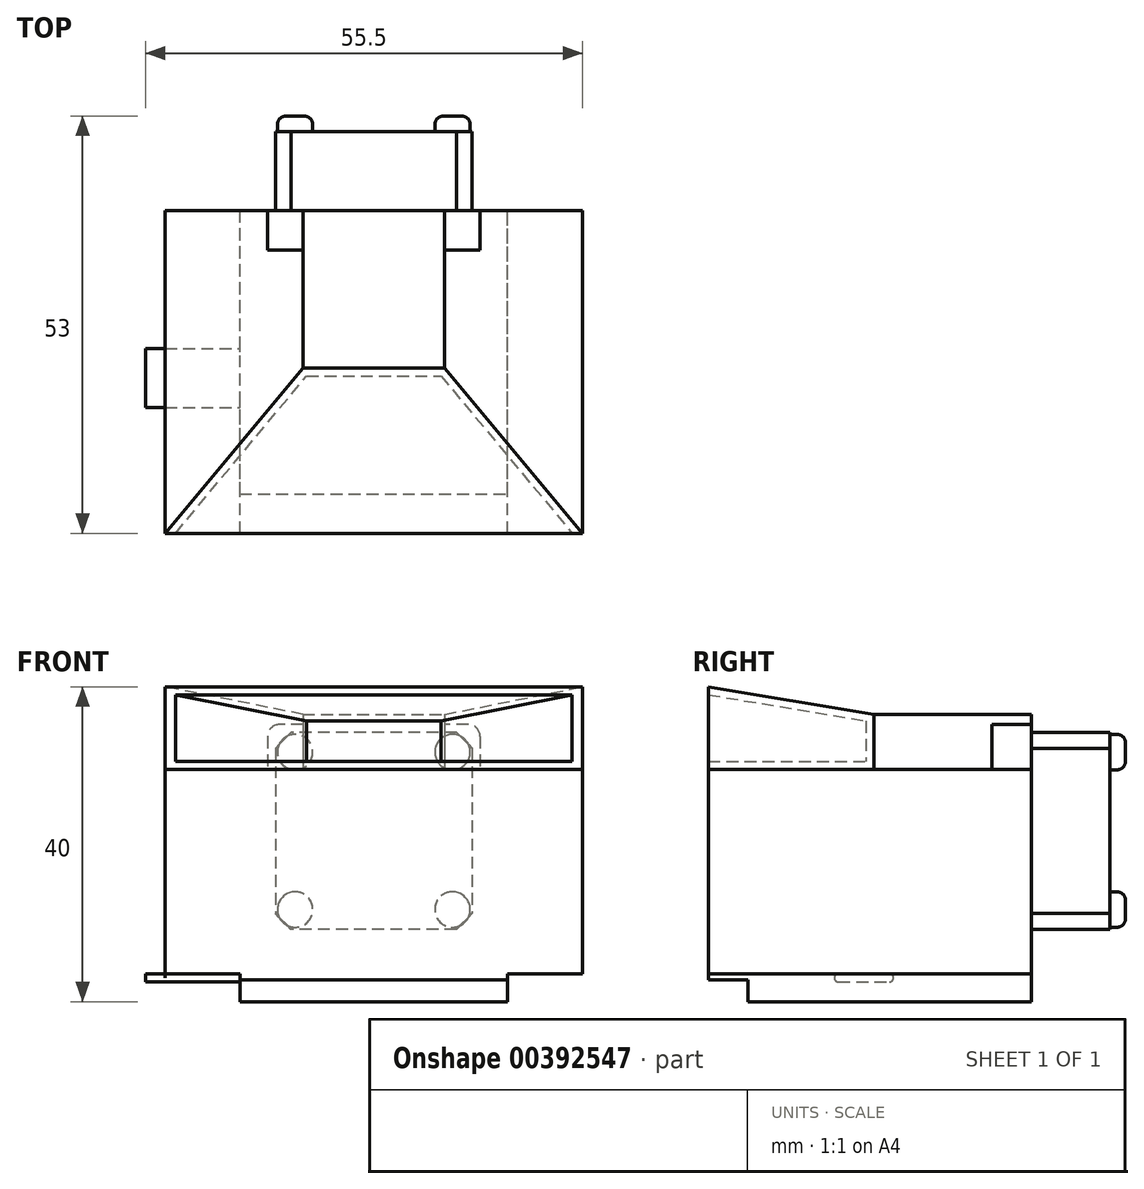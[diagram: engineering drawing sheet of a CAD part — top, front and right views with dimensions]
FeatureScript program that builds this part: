
annotation { "Feature Type Name" : "Feature", "Feature Type Description" : "" }
export const myFeature = defineFeature(function(context is Context, id is Id, definition is map)
    precondition{}
    {
        {
            var Q0;
            Q0=qCreatedBy(makeId("Front.planeOp"),FACE);
            var sketch = newSketch(context, id + "F0", { "sketchPlane" : qUnion([Q0])});
            skLineSegment(sketch, "E0.bottom", {"start": v(-26.5, -13) * mm, "end": v(26.5, -13) * mm});
            skLineSegment(sketch, "E0.top", {"start": v(-26.5, 13) * mm, "end": v(26.5, 13) * mm});
            skLineSegment(sketch, "E0.left", {"start": v(-26.5, -13) * mm, "end": v(-26.5, 13) * mm});
            skLineSegment(sketch, "E0.right", {"start": v(26.5, -13) * mm, "end": v(26.5, 13) * mm});
            skPoint(sketch, "E1", {"position": v(-26.5, 0) * mm});
            skPoint(sketch, "E2", {"position": v(0, -13) * mm});
            skSolve(sketch);
        }
        {
            var Q0;
            {var subQ0=sQuery(id+"F0.wireOp",EDGE,"lT0iIPiZ-68E4-k4fb-Xnzf-Mz2QpFusgy4Y.top");Q0=makeQuery(id+"F0.imprint","IMPRINT",FACE,{"disambiguationData":[TD([[makeQuery(id+"F0.imprint","IMPRINT",EDGE,{"derivedFrom":subQ0}),1.0]])]});}
            var Q1;
            Q1=makeQuery(id+"F0.imprint","IMPRINT",FACE,{"disambiguationData":[TD([[makeQuery(id+"F0.imprint","IMPRINT",EDGE,{"derivedFrom":sQuery(id+"F0.wireOp",EDGE,"E0.bottom")}),1.0]])]});
            extrude(context, id + "F1", {"entities" : qUnion([Q0, Q1]), "oppositeDirection" : true, "depth" : 41 * mm});
        }
        {
            var Q0;
            Q0=makeQuery(id+"F1.opExtrude","SWEPT_FACE",FACE,{"disambiguationData":[OSD([sQuery(id+"F0.wireOp",EDGE,"E0.top")])]});
            var sketch = newSketch(context, id + "F2", { "sketchPlane" : qUnion([Q0])});
            skLineSegment(sketch, "E3.bottom", {"start": v(-9, 41) * mm, "end": v(9, 41) * mm});
            skLineSegment(sketch, "E3.top", {"start": v(-9, 21) * mm, "end": v(9, 21) * mm});
            skLineSegment(sketch, "E3.left", {"start": v(-9, 41) * mm, "end": v(-9, 21) * mm});
            skLineSegment(sketch, "E3.right", {"start": v(9, 41) * mm, "end": v(9, 21) * mm});
            skPoint(sketch, "E4", {"position": v(0, 41) * mm});
            skSolve(sketch);
        }
        {
            var Q0;
            Q0=makeQuery(id+"F2.imprint","IMPRINT",FACE,{"disambiguationData":[TD([[makeQuery(id+"F2.imprint","IMPRINT",EDGE,{"derivedFrom":sQuery(id+"F2.wireOp",EDGE,"E3.bottom")}),-1.0]])]});
            extrude(context, id + "F3", {"entities" : qUnion([Q0]), "operationType" : NewBodyOperationType.ADD, "depth" : 7 * mm});
        }
        {
            var Q0;
            Q0=makeQuery(id+"F0.imprint","IMPRINT",FACE,{"disambiguationData":[TD([[makeQuery(id+"F0.imprint","IMPRINT",EDGE,{"derivedFrom":sQuery(id+"F0.wireOp",EDGE,"E0.bottom")}),1.0]])]});
            var sketch = newSketch(context, id + "F4", { "sketchPlane" : qUnion([Q0])});
            skLineSegment(sketch, "E5.bottom", {"start": v(-26.5, 13) * mm, "end": v(26.5, 13) * mm});
            skLineSegment(sketch, "E5.top", {"start": v(-26.5, 23.5) * mm, "end": v(26.5, 23.5) * mm});
            skLineSegment(sketch, "E5.left", {"start": v(-26.5, 13) * mm, "end": v(-26.5, 23.5) * mm});
            skLineSegment(sketch, "E5.right", {"start": v(26.5, 13) * mm, "end": v(26.5, 23.5) * mm});
            skSolve(sketch);
        }
        {
            var Q1;
            Q1=makeQuery(id+"F3.opExtrude","SWEPT_FACE",FACE,{"disambiguationData":[OSD([sQuery(id+"F2.wireOp",EDGE,"E3.top")])]});
            var Q2;
            Q2=makeQuery(id+"F4.imprint","IMPRINT",FACE,{"disambiguationData":[TD([[makeQuery(id+"F4.imprint","IMPRINT",EDGE,{"derivedFrom":sQuery(id+"F4.wireOp",EDGE,"E5.bottom")}),1.0]])]});
            loft(context, id + "F5", {"sheetProfilesArray" : [{ "sheetProfileEntities" : qUnion([Q1]) }, { "sheetProfileEntities" : qUnion([Q2]) }]});
        }
        {
            var Q0;
            Q0=makeQuery(id+"F5.opLoft","CAP_FACE",FACE,{"disambiguationData":[OSD([makeQuery(id+"F4.imprint","IMPRINT",FACE,{"disambiguationData":[TD([[makeQuery(id+"F4.imprint","IMPRINT",EDGE,{"derivedFrom":sQuery(id+"F4.wireOp",EDGE,"E5.bottom")}),1.0]])]})])],"isStart":true});
            shell(context, id + "F6", {"entities" : qUnion([Q0]), "thickness" : 1 * mm});
        }
        {
            var Q0;
            Q0=makeQuery(id+"F1.opExtrude","SWEPT_FACE",FACE,{"disambiguationData":[OSD([sQuery(id+"F0.wireOp",EDGE,"E0.bottom")])]});
            var sketch = newSketch(context, id + "F7", { "sketchPlane" : qUnion([Q0])});
            skLineSegment(sketch, "E6.bottom", {"start": v(-17, 0) * mm, "end": v(17, 0) * mm});
            skLineSegment(sketch, "E6.top", {"start": v(-17, -5) * mm, "end": v(17, -5) * mm});
            skLineSegment(sketch, "E6.left", {"start": v(-17, 0) * mm, "end": v(-17, -5) * mm});
            skLineSegment(sketch, "E6.right", {"start": v(17, 0) * mm, "end": v(17, -5) * mm});
            skLineSegment(sketch, "E7.top", {"start": v(-17, -41) * mm, "end": v(17, -41) * mm});
            skLineSegment(sketch, "E7.left", {"start": v(-17, -5) * mm, "end": v(-17, -41) * mm});
            skLineSegment(sketch, "E7.right", {"start": v(17, -5) * mm, "end": v(17, -41) * mm});
            skPoint(sketch, "E8", {"position": v(0, 0) * mm});
            skSolve(sketch);
        }
        {
            var Q0;
            Q0=makeQuery(id+"F7.imprint","IMPRINT",FACE,{"disambiguationData":[TD([[makeQuery(id+"F7.imprint","IMPRINT",EDGE,{"derivedFrom":sQuery(id+"F7.wireOp",EDGE,"E6.bottom")}),-1.0]])]});
            extrude(context, id + "F8", {"entities" : qUnion([Q0]), "operationType" : NewBodyOperationType.ADD, "depth" : 0.7 * mm});
        }
        {
            var Q0;
            Q0=makeQuery(id+"F7.imprint","IMPRINT",FACE,{"disambiguationData":[TD([[makeQuery(id+"F7.imprint","IMPRINT",EDGE,{"derivedFrom":sQuery(id+"F7.wireOp",EDGE,"E6.top")}),-1.0]])]});
            extrude(context, id + "F9", {"entities" : qUnion([Q0]), "operationType" : NewBodyOperationType.ADD, "depth" : 3.5 * mm});
        }
        {
            var Q0;
            Q0=makeQuery(id+"F9.boolean.opBoolean","MERGE",FACE,{"derivedFrom":[makeQuery(id+"F3.boolean.opBoolean","MERGE",FACE,{"derivedFrom":[makeQuery(id+"F1.opExtrude","CAP_FACE",FACE,{"disambiguationData":[OSD([sQuery(id+"F0.wireOp",EDGE,"E0.bottom"),sQuery(id+"F0.wireOp",EDGE,"E0.top"),sQuery(id+"F0.wireOp",EDGE,"E0.left"),sQuery(id+"F0.wireOp",EDGE,"E0.right")])],"isStart":false}),makeQuery(id+"F3.opExtrude","SWEPT_FACE",FACE,{"disambiguationData":[OSD([sQuery(id+"F2.wireOp",EDGE,"E3.bottom")])]})]}),makeQuery(id+"F9.opExtrude","SWEPT_FACE",FACE,{"disambiguationData":[OSD([sQuery(id+"F7.wireOp",EDGE,"E7.top")])]})]});
            var sketch = newSketch(context, id + "F10", { "sketchPlane" : qUnion([Q0])});
            skLineSegment(sketch, "E9.bottom", {"start": v(-12.5, 17.7) * mm, "end": v(12.5, 17.7) * mm});
            skLineSegment(sketch, "E9.top", {"start": v(-12.5, -7.3) * mm, "end": v(12.5, -7.3) * mm});
            skLineSegment(sketch, "E9.left", {"start": v(-12.5, 17.7) * mm, "end": v(-12.5, -7.3) * mm});
            skLineSegment(sketch, "E9.right", {"start": v(12.5, 17.7) * mm, "end": v(12.5, -7.3) * mm});
            skPoint(sketch, "E10", {"position": v(0, -7.3) * mm});
            skLineSegment(sketch, "E11.0", {"start": v(-13.5, 18.7) * mm, "end": v(-13.5, -8.3) * mm});
            skLineSegment(sketch, "E11.1", {"start": v(-13.5, 18.7) * mm, "end": v(13.5, 18.7) * mm});
            skLineSegment(sketch, "E11.2", {"start": v(13.5, 18.7) * mm, "end": v(13.5, -8.3) * mm});
            skLineSegment(sketch, "E11.3", {"start": v(-13.5, -8.3) * mm, "end": v(13.5, -8.3) * mm});
            skSolve(sketch);
        }
        {
            var Q0;
            {var subQ0=sQuery(id+"F10.wireOp",EDGE,"E9.right");var subQ1=sQuery(id+"F10.wireOp",EDGE,"E9.bottom");var subQ2=makeQuery(id+"F10.imprint","INTERSECT",VERTEX,{"derivedFrom":[subQ1,subQ0]});Q0=makeQuery(id+"F10.imprint","IMPRINT",FACE,{"disambiguationData":[TD([[makeQuery(id+"F10.imprint","IMPRINT",EDGE,{"disambiguationData":[TD([[subQ2,1.0]])],"derivedFrom":subQ1}),-1.0]])]});}
            var Q1;
            {var subQ1=sQuery(id+"F10.wireOp",EDGE,"E9.top");Q1=makeQuery(id+"F10.imprint","IMPRINT",FACE,{"disambiguationData":[TD([[makeQuery(id+"F10.imprint","IMPRINT",EDGE,{"derivedFrom":subQ1}),1.0]])]});}
            var Q2;
            {var subQ0=sQuery(id+"F10.wireOp",EDGE,"E9.left");var subQ1=sQuery(id+"F10.wireOp",EDGE,"E9.bottom");var subQ2=makeQuery(id+"F10.imprint","INTERSECT",VERTEX,{"derivedFrom":[subQ1,subQ0]});Q2=makeQuery(id+"F10.imprint","IMPRINT",FACE,{"disambiguationData":[TD([[makeQuery(id+"F10.imprint","IMPRINT",EDGE,{"disambiguationData":[TD([[subQ2,-1.0]])],"derivedFrom":subQ1}),-1.0]])]});}
            extrude(context, id + "F11", {"entities" : qUnion([Q0, Q1, Q2]), "operationType" : NewBodyOperationType.ADD, "depth" : 10 * mm});
        }
        {
            var Q0;
            Q0=makeQuery(id+"F11.opExtrude","SWEPT_EDGE",EDGE,{"disambiguationData":[OSD([sQuery(id+"F10.wireOp",EDGE,"E9.bottom"),sQuery(id+"F10.wireOp",EDGE,"E9.left")])]});
            var Q1;
            Q1=makeQuery(id+"F11.opExtrude","SWEPT_EDGE",EDGE,{"disambiguationData":[OSD([sQuery(id+"F10.wireOp",EDGE,"E9.bottom"),sQuery(id+"F10.wireOp",EDGE,"E9.right")])]});
            var Q2;
            Q2=makeQuery(id+"F11.opExtrude","SWEPT_EDGE",EDGE,{"disambiguationData":[OSD([sQuery(id+"F10.wireOp",EDGE,"E9.top"),sQuery(id+"F10.wireOp",EDGE,"E9.right")])]});
            var Q3;
            Q3=makeQuery(id+"F11.opExtrude","SWEPT_EDGE",EDGE,{"disambiguationData":[OSD([sQuery(id+"F10.wireOp",EDGE,"E9.top"),sQuery(id+"F10.wireOp",EDGE,"E9.left")])]});
            chamfer(context, id + "F12", {"entities" : qUnion([Q0, Q1, Q2, Q3]), "width" : 2 * mm, "tangentPropagation" : true});
        }
        {
            var Q0;
            {var subQ11=sQuery(id+"F10.wireOp",EDGE,"E9.left");var subQ13=sQuery(id+"F10.wireOp",EDGE,"E9.bottom");var subQ14=makeQuery(id+"F10.imprint","INTERSECT",VERTEX,{"derivedFrom":[subQ13,subQ11]});Q0=makeQuery(id+"F10.imprint","IMPRINT",FACE,{"disambiguationData":[TD([[makeQuery(id+"F10.imprint","IMPRINT",EDGE,{"disambiguationData":[TD([[subQ14,-1.0]])],"derivedFrom":subQ13}),1.0]])]});}
            var Q1;
            {var subQ0=sQuery(id+"F10.wireOp",EDGE,"E9.left");var subQ1=sQuery(id+"F10.wireOp",EDGE,"E9.bottom");var subQ2=makeQuery(id+"F10.imprint","INTERSECT",VERTEX,{"derivedFrom":[subQ1,subQ0]});Q1=makeQuery(id+"F10.imprint","IMPRINT",FACE,{"disambiguationData":[TD([[makeQuery(id+"F10.imprint","IMPRINT",EDGE,{"disambiguationData":[TD([[subQ2,-1.0]])],"derivedFrom":subQ1}),-1.0]])]});}
            var Q2;
            {var subQ11=sQuery(id+"F10.wireOp",EDGE,"E9.right");var subQ12=sQuery(id+"F10.wireOp",EDGE,"E9.bottom");var subQ13=makeQuery(id+"F10.imprint","INTERSECT",VERTEX,{"derivedFrom":[subQ12,subQ11]});Q2=makeQuery(id+"F10.imprint","IMPRINT",FACE,{"disambiguationData":[TD([[makeQuery(id+"F10.imprint","IMPRINT",EDGE,{"disambiguationData":[TD([[subQ13,1.0]])],"derivedFrom":subQ12}),1.0]])]});}
            var Q3;
            {var subQ0=sQuery(id+"F10.wireOp",EDGE,"E9.right");var subQ1=sQuery(id+"F10.wireOp",EDGE,"E9.bottom");var subQ2=makeQuery(id+"F10.imprint","INTERSECT",VERTEX,{"derivedFrom":[subQ1,subQ0]});Q3=makeQuery(id+"F10.imprint","IMPRINT",FACE,{"disambiguationData":[TD([[makeQuery(id+"F10.imprint","IMPRINT",EDGE,{"disambiguationData":[TD([[subQ2,1.0]])],"derivedFrom":subQ1}),-1.0]])]});}
            extrude(context, id + "F13", {"entities" : qUnion([Q0, Q1, Q2, Q3]), "operationType" : NewBodyOperationType.ADD, "oppositeDirection" : true, "depth" : 5 * mm});
        }
        {
            var Q0;
            Q0=makeQuery(id+"F13.opExtrude","SWEPT_EDGE",EDGE,{"disambiguationData":[OSD([sQuery(id+"F10.wireOp",EDGE,"E11.0"),sQuery(id+"F10.wireOp",EDGE,"E11.1")])]});
            var Q1;
            Q1=makeQuery(id+"F13.opExtrude","SWEPT_EDGE",EDGE,{"disambiguationData":[OSD([sQuery(id+"F10.wireOp",EDGE,"E11.1"),sQuery(id+"F10.wireOp",EDGE,"E11.2")])]});
            fillet(context, id + "F14", {"entities" : qUnion([Q0, Q1]), "radius" : 1.5 * mm, "tangentPropagation" : true, "allowEdgeOverflow" : false});
        }
        {
            var Q0;
            Q0=makeQuery(id+"F11.opExtrude","CAP_FACE",FACE,{"disambiguationData":[OSD([sQuery(id+"F10.wireOp",EDGE,"E9.bottom"),sQuery(id+"F10.wireOp",EDGE,"E9.top"),sQuery(id+"F10.wireOp",EDGE,"E9.left"),sQuery(id+"F10.wireOp",EDGE,"E9.right")])],"isStart":false});
            var sketch = newSketch(context, id + "F15", { "sketchPlane" : qUnion([Q0])});
            skLineSegment(sketch, "E12.bottom", {"start": v(-10, 15.2) * mm, "end": v(10, 15.2) * mm, "construction": true});
            skLineSegment(sketch, "E12.top", {"start": v(-10, -4.8) * mm, "end": v(10, -4.8) * mm, "construction": true});
            skLineSegment(sketch, "E12.left", {"start": v(-10, 15.2) * mm, "end": v(-10, -4.8) * mm, "construction": true});
            skLineSegment(sketch, "E12.right", {"start": v(10, 15.2) * mm, "end": v(10, -4.8) * mm, "construction": true});
            skPoint(sketch, "E13", {"position": v(0, 15.2) * mm});
            skPoint(sketch, "E14", {"position": v(-10, 5.2) * mm});
            skPoint(sketch, "E15", {"position": v(0, 17.7) * mm});
            skPoint(sketch, "E16", {"position": v(-12.5, 5.2) * mm});
            skCircle(sketch, "E17", {"center": v(-10, 15.2) * mm, "radius": 2.25 * mm});
            skCircle(sketch, "E18", {"center": v(10, 15.2) * mm, "radius": 2.25 * mm});
            skCircle(sketch, "E19", {"center": v(-10, -4.8) * mm, "radius": 2.25 * mm});
            skCircle(sketch, "E20", {"center": v(10, -4.8) * mm, "radius": 2.25 * mm});
            skSolve(sketch);
        }
        {
            var Q0;
            {var subQ0=sQuery(id+"F15.wireOp",EDGE,"E17");var subQ1=sQuery(id+"F10.wireOp",EDGE,"E9.left");var subQ2=sQuery(id+"F10.wireOp",EDGE,"E9.bottom");var subQ3=makeQuery(id+"F12.opChamfer","BLEND_EDGE",EDGE,{"blendedFrom":[makeQuery(id+"F11.opExtrude","SWEPT_EDGE",EDGE,{"disambiguationData":[OSD([subQ2,subQ1])]}),makeQuery(id+"F11.opExtrude","CAP_FACE",FACE,{"disambiguationData":[OSD([subQ2,sQuery(id+"F10.wireOp",EDGE,"E9.top"),subQ1,sQuery(id+"F10.wireOp",EDGE,"E9.right")])],"isStart":false})],"blendedInto":[makeQuery(id+"F11.opExtrude","CAP_FACE",FACE,{"disambiguationData":[OSD([subQ2,sQuery(id+"F10.wireOp",EDGE,"E9.top"),subQ1,sQuery(id+"F10.wireOp",EDGE,"E9.right")])],"isStart":false})]});var subQ4=makeQuery(id+"F15.imprint","INTERSECT",VERTEX,{"disambiguationData":[OD(0.0)],"derivedFrom":[subQ3,subQ0]});Q0=makeQuery(id+"F15.imprint","IMPRINT",FACE,{"disambiguationData":[TD([[makeQuery(id+"F15.imprint","IMPRINT",EDGE,{"disambiguationData":[TD([[subQ4,1.0]])],"derivedFrom":subQ0}),1.0]])]});}
            var Q1;
            {var subQ0=sQuery(id+"F15.wireOp",EDGE,"E18");var subQ1=sQuery(id+"F10.wireOp",EDGE,"E9.right");var subQ2=sQuery(id+"F10.wireOp",EDGE,"E9.bottom");var subQ3=makeQuery(id+"F12.opChamfer","BLEND_EDGE",EDGE,{"blendedFrom":[makeQuery(id+"F11.opExtrude","SWEPT_EDGE",EDGE,{"disambiguationData":[OSD([subQ2,subQ1])]}),makeQuery(id+"F11.opExtrude","CAP_FACE",FACE,{"disambiguationData":[OSD([subQ2,sQuery(id+"F10.wireOp",EDGE,"E9.top"),sQuery(id+"F10.wireOp",EDGE,"E9.left"),subQ1])],"isStart":false})],"blendedInto":[makeQuery(id+"F11.opExtrude","CAP_FACE",FACE,{"disambiguationData":[OSD([subQ2,sQuery(id+"F10.wireOp",EDGE,"E9.top"),sQuery(id+"F10.wireOp",EDGE,"E9.left"),subQ1])],"isStart":false})]});var subQ4=makeQuery(id+"F15.imprint","INTERSECT",VERTEX,{"disambiguationData":[OD(0.0)],"derivedFrom":[subQ3,subQ0]});Q1=makeQuery(id+"F15.imprint","IMPRINT",FACE,{"disambiguationData":[TD([[makeQuery(id+"F15.imprint","IMPRINT",EDGE,{"disambiguationData":[TD([[subQ4,-1.0]])],"derivedFrom":subQ0}),1.0]])]});}
            var Q2;
            {var subQ0=sQuery(id+"F15.wireOp",EDGE,"E20");var subQ1=sQuery(id+"F10.wireOp",EDGE,"E9.right");var subQ2=sQuery(id+"F10.wireOp",EDGE,"E9.top");var subQ3=makeQuery(id+"F12.opChamfer","BLEND_EDGE",EDGE,{"blendedFrom":[makeQuery(id+"F11.opExtrude","SWEPT_EDGE",EDGE,{"disambiguationData":[OSD([subQ2,subQ1])]}),makeQuery(id+"F11.opExtrude","CAP_FACE",FACE,{"disambiguationData":[OSD([sQuery(id+"F10.wireOp",EDGE,"E9.bottom"),subQ2,sQuery(id+"F10.wireOp",EDGE,"E9.left"),subQ1])],"isStart":false})],"blendedInto":[makeQuery(id+"F11.opExtrude","CAP_FACE",FACE,{"disambiguationData":[OSD([sQuery(id+"F10.wireOp",EDGE,"E9.bottom"),subQ2,sQuery(id+"F10.wireOp",EDGE,"E9.left"),subQ1])],"isStart":false})]});var subQ4=makeQuery(id+"F15.imprint","INTERSECT",VERTEX,{"disambiguationData":[OD(0.0)],"derivedFrom":[subQ3,subQ0]});Q2=makeQuery(id+"F15.imprint","IMPRINT",FACE,{"disambiguationData":[TD([[makeQuery(id+"F15.imprint","IMPRINT",EDGE,{"disambiguationData":[TD([[subQ4,1.0]])],"derivedFrom":subQ0}),1.0]])]});}
            var Q3;
            {var subQ0=sQuery(id+"F15.wireOp",EDGE,"E19");var subQ1=sQuery(id+"F10.wireOp",EDGE,"E9.left");var subQ2=sQuery(id+"F10.wireOp",EDGE,"E9.top");var subQ3=makeQuery(id+"F12.opChamfer","BLEND_EDGE",EDGE,{"blendedFrom":[makeQuery(id+"F11.opExtrude","SWEPT_EDGE",EDGE,{"disambiguationData":[OSD([subQ2,subQ1])]}),makeQuery(id+"F11.opExtrude","CAP_FACE",FACE,{"disambiguationData":[OSD([sQuery(id+"F10.wireOp",EDGE,"E9.bottom"),subQ2,subQ1,sQuery(id+"F10.wireOp",EDGE,"E9.right")])],"isStart":false})],"blendedInto":[makeQuery(id+"F11.opExtrude","CAP_FACE",FACE,{"disambiguationData":[OSD([sQuery(id+"F10.wireOp",EDGE,"E9.bottom"),subQ2,subQ1,sQuery(id+"F10.wireOp",EDGE,"E9.right")])],"isStart":false})]});var subQ4=makeQuery(id+"F15.imprint","INTERSECT",VERTEX,{"disambiguationData":[OD(0.0)],"derivedFrom":[subQ3,subQ0]});Q3=makeQuery(id+"F15.imprint","IMPRINT",FACE,{"disambiguationData":[TD([[makeQuery(id+"F15.imprint","IMPRINT",EDGE,{"disambiguationData":[TD([[subQ4,-1.0]])],"derivedFrom":subQ0}),1.0]])]});}
            var Q4;
            {var subQ0=sQuery(id+"F15.wireOp",EDGE,"E17");var subQ1=sQuery(id+"F10.wireOp",EDGE,"E9.left");var subQ2=sQuery(id+"F10.wireOp",EDGE,"E9.bottom");var subQ3=makeQuery(id+"F12.opChamfer","BLEND_EDGE",EDGE,{"blendedFrom":[makeQuery(id+"F11.opExtrude","SWEPT_EDGE",EDGE,{"disambiguationData":[OSD([subQ2,subQ1])]}),makeQuery(id+"F11.opExtrude","CAP_FACE",FACE,{"disambiguationData":[OSD([subQ2,sQuery(id+"F10.wireOp",EDGE,"E9.top"),subQ1,sQuery(id+"F10.wireOp",EDGE,"E9.right")])],"isStart":false})],"blendedInto":[makeQuery(id+"F11.opExtrude","CAP_FACE",FACE,{"disambiguationData":[OSD([subQ2,sQuery(id+"F10.wireOp",EDGE,"E9.top"),subQ1,sQuery(id+"F10.wireOp",EDGE,"E9.right")])],"isStart":false})]});var subQ4=makeQuery(id+"F15.imprint","INTERSECT",VERTEX,{"disambiguationData":[OD(0.0)],"derivedFrom":[subQ3,subQ0]});Q4=makeQuery(id+"F15.imprint","IMPRINT",FACE,{"disambiguationData":[TD([[makeQuery(id+"F15.imprint","IMPRINT",EDGE,{"disambiguationData":[TD([[subQ4,-1.0]])],"derivedFrom":subQ0}),1.0]])]});}
            var Q5;
            {var subQ0=sQuery(id+"F15.wireOp",EDGE,"E19");var subQ1=sQuery(id+"F10.wireOp",EDGE,"E9.left");var subQ2=sQuery(id+"F10.wireOp",EDGE,"E9.top");var subQ3=makeQuery(id+"F12.opChamfer","BLEND_EDGE",EDGE,{"blendedFrom":[makeQuery(id+"F11.opExtrude","SWEPT_EDGE",EDGE,{"disambiguationData":[OSD([subQ2,subQ1])]}),makeQuery(id+"F11.opExtrude","CAP_FACE",FACE,{"disambiguationData":[OSD([sQuery(id+"F10.wireOp",EDGE,"E9.bottom"),subQ2,subQ1,sQuery(id+"F10.wireOp",EDGE,"E9.right")])],"isStart":false})],"blendedInto":[makeQuery(id+"F11.opExtrude","CAP_FACE",FACE,{"disambiguationData":[OSD([sQuery(id+"F10.wireOp",EDGE,"E9.bottom"),subQ2,subQ1,sQuery(id+"F10.wireOp",EDGE,"E9.right")])],"isStart":false})]});var subQ4=makeQuery(id+"F15.imprint","INTERSECT",VERTEX,{"disambiguationData":[OD(0.0)],"derivedFrom":[subQ3,subQ0]});Q5=makeQuery(id+"F15.imprint","IMPRINT",FACE,{"disambiguationData":[TD([[makeQuery(id+"F15.imprint","IMPRINT",EDGE,{"disambiguationData":[TD([[subQ4,1.0]])],"derivedFrom":subQ0}),1.0]])]});}
            var Q6;
            {var subQ0=sQuery(id+"F15.wireOp",EDGE,"E20");var subQ1=sQuery(id+"F10.wireOp",EDGE,"E9.right");var subQ2=sQuery(id+"F10.wireOp",EDGE,"E9.top");var subQ3=makeQuery(id+"F12.opChamfer","BLEND_EDGE",EDGE,{"blendedFrom":[makeQuery(id+"F11.opExtrude","SWEPT_EDGE",EDGE,{"disambiguationData":[OSD([subQ2,subQ1])]}),makeQuery(id+"F11.opExtrude","CAP_FACE",FACE,{"disambiguationData":[OSD([sQuery(id+"F10.wireOp",EDGE,"E9.bottom"),subQ2,sQuery(id+"F10.wireOp",EDGE,"E9.left"),subQ1])],"isStart":false})],"blendedInto":[makeQuery(id+"F11.opExtrude","CAP_FACE",FACE,{"disambiguationData":[OSD([sQuery(id+"F10.wireOp",EDGE,"E9.bottom"),subQ2,sQuery(id+"F10.wireOp",EDGE,"E9.left"),subQ1])],"isStart":false})]});var subQ4=makeQuery(id+"F15.imprint","INTERSECT",VERTEX,{"disambiguationData":[OD(0.0)],"derivedFrom":[subQ3,subQ0]});Q6=makeQuery(id+"F15.imprint","IMPRINT",FACE,{"disambiguationData":[TD([[makeQuery(id+"F15.imprint","IMPRINT",EDGE,{"disambiguationData":[TD([[subQ4,-1.0]])],"derivedFrom":subQ0}),1.0]])]});}
            var Q7;
            {var subQ0=sQuery(id+"F15.wireOp",EDGE,"E18");var subQ1=sQuery(id+"F10.wireOp",EDGE,"E9.right");var subQ2=sQuery(id+"F10.wireOp",EDGE,"E9.bottom");var subQ3=makeQuery(id+"F12.opChamfer","BLEND_EDGE",EDGE,{"blendedFrom":[makeQuery(id+"F11.opExtrude","SWEPT_EDGE",EDGE,{"disambiguationData":[OSD([subQ2,subQ1])]}),makeQuery(id+"F11.opExtrude","CAP_FACE",FACE,{"disambiguationData":[OSD([subQ2,sQuery(id+"F10.wireOp",EDGE,"E9.top"),sQuery(id+"F10.wireOp",EDGE,"E9.left"),subQ1])],"isStart":false})],"blendedInto":[makeQuery(id+"F11.opExtrude","CAP_FACE",FACE,{"disambiguationData":[OSD([subQ2,sQuery(id+"F10.wireOp",EDGE,"E9.top"),sQuery(id+"F10.wireOp",EDGE,"E9.left"),subQ1])],"isStart":false})]});var subQ4=makeQuery(id+"F15.imprint","INTERSECT",VERTEX,{"disambiguationData":[OD(0.0)],"derivedFrom":[subQ3,subQ0]});Q7=makeQuery(id+"F15.imprint","IMPRINT",FACE,{"disambiguationData":[TD([[makeQuery(id+"F15.imprint","IMPRINT",EDGE,{"disambiguationData":[TD([[subQ4,1.0]])],"derivedFrom":subQ0}),1.0]])]});}
            extrude(context, id + "F16", {"entities" : qUnion([Q0, Q1, Q2, Q3, Q4, Q5, Q6, Q7]), "operationType" : NewBodyOperationType.ADD, "depth" : 2 * mm});
        }
        {
            var Q0;
            Q0=makeQuery(id+"F16.opExtrude","CAP_EDGE",EDGE,{"disambiguationData":[OSD([sQuery(id+"F15.wireOp",EDGE,"E17")])],"isStart":false});
            var Q1;
            Q1=makeQuery(id+"F16.opExtrude","CAP_EDGE",EDGE,{"disambiguationData":[OSD([sQuery(id+"F15.wireOp",EDGE,"E18")])],"isStart":false});
            var Q2;
            Q2=makeQuery(id+"F16.opExtrude","CAP_EDGE",EDGE,{"disambiguationData":[OSD([sQuery(id+"F15.wireOp",EDGE,"E19")])],"isStart":false});
            var Q3;
            Q3=makeQuery(id+"F16.opExtrude","CAP_EDGE",EDGE,{"disambiguationData":[OSD([sQuery(id+"F15.wireOp",EDGE,"E20")])],"isStart":false});
            fillet(context, id + "F17", {"entities" : qUnion([Q0, Q1, Q2, Q3]), "radius" : 1.1 * mm, "tangentPropagation" : true, "allowEdgeOverflow" : false});
        }
        {
            var Q0;
            Q0=makeQuery(id+"F9.boolean.opBoolean","MERGE",FACE,{"derivedFrom":[makeQuery(id+"F8.opExtrude","SWEPT_FACE",FACE,{"disambiguationData":[OSD([sQuery(id+"F7.wireOp",EDGE,"E6.left")])]}),makeQuery(id+"F9.opExtrude","SWEPT_FACE",FACE,{"disambiguationData":[OSD([sQuery(id+"F7.wireOp",EDGE,"E7.left")])]})]});
            var sketch = newSketch(context, id + "F18", { "sketchPlane" : qUnion([Q0])});
            skLineSegment(sketch, "E21.bottom", {"start": v(-16, -13) * mm, "end": v(-23.5, -13) * mm});
            skLineSegment(sketch, "E21.top", {"start": v(-16, -14) * mm, "end": v(-23.5, -14) * mm});
            skLineSegment(sketch, "E21.left", {"start": v(-16, -13) * mm, "end": v(-16, -14) * mm});
            skLineSegment(sketch, "E21.right", {"start": v(-23.5, -13) * mm, "end": v(-23.5, -14) * mm});
            skSolve(sketch);
        }
        {
            var Q0;
            Q0=makeQuery(id+"F18.imprint","IMPRINT",FACE,{"disambiguationData":[TD([[makeQuery(id+"F18.imprint","IMPRINT",EDGE,{"derivedFrom":sQuery(id+"F18.wireOp",EDGE,"E21.bottom")}),1.0]])]});
            extrude(context, id + "F19", {"entities" : qUnion([Q0]), "operationType" : NewBodyOperationType.ADD, "depth" : 12 * mm});
        }
        {
            var Q0;
            Q0=makeQuery(id+"F19.opExtrude","SWEPT_EDGE",EDGE,{"disambiguationData":[OSD([sQuery(id+"F18.wireOp",EDGE,"E21.top"),sQuery(id+"F18.wireOp",EDGE,"E21.left")])]});
            var Q1;
            {var subQ0=sQuery(id+"F18.wireOp",EDGE,"E21.left");var subQ1=sQuery(id+"F18.wireOp",EDGE,"E21.bottom");Q1=makeQuery(id+"F19.boolean.opBoolean","SPLIT",EDGE,{"disambiguationData":[TD([makeQuery(id+"F19.opExtrude","CAP_FACE",FACE,{"disambiguationData":[OSD([subQ1,sQuery(id+"F18.wireOp",EDGE,"E21.top"),subQ0,sQuery(id+"F18.wireOp",EDGE,"E21.right")])],"isStart":false})])],"derivedFrom":makeQuery(id+"F19.opExtrude","SWEPT_EDGE",EDGE,{"disambiguationData":[OSD([sQuery(id+"F7.wireOp",EDGE,"E6.left"),sQuery(id+"F7.wireOp",EDGE,"E7.left"),subQ1,subQ0])]})});}
            var Q2;
            Q2=makeQuery(id+"F19.opExtrude","SWEPT_EDGE",EDGE,{"disambiguationData":[OSD([sQuery(id+"F18.wireOp",EDGE,"E21.top"),sQuery(id+"F18.wireOp",EDGE,"E21.right")])]});
            var Q3;
            {var subQ0=sQuery(id+"F18.wireOp",EDGE,"E21.right");var subQ1=sQuery(id+"F18.wireOp",EDGE,"E21.bottom");Q3=makeQuery(id+"F19.boolean.opBoolean","SPLIT",EDGE,{"disambiguationData":[TD([makeQuery(id+"F19.opExtrude","CAP_FACE",FACE,{"disambiguationData":[OSD([subQ1,sQuery(id+"F18.wireOp",EDGE,"E21.top"),sQuery(id+"F18.wireOp",EDGE,"E21.left"),subQ0])],"isStart":false})])],"derivedFrom":makeQuery(id+"F19.opExtrude","SWEPT_EDGE",EDGE,{"disambiguationData":[OSD([sQuery(id+"F7.wireOp",EDGE,"E6.left"),sQuery(id+"F7.wireOp",EDGE,"E7.left"),subQ1,subQ0])]})});}
            fillet(context, id + "F20", {"entities" : qUnion([Q0, Q1, Q2, Q3]), "radius" : 0.5 * mm, "tangentPropagation" : true, "allowEdgeOverflow" : false});
        }
    });
